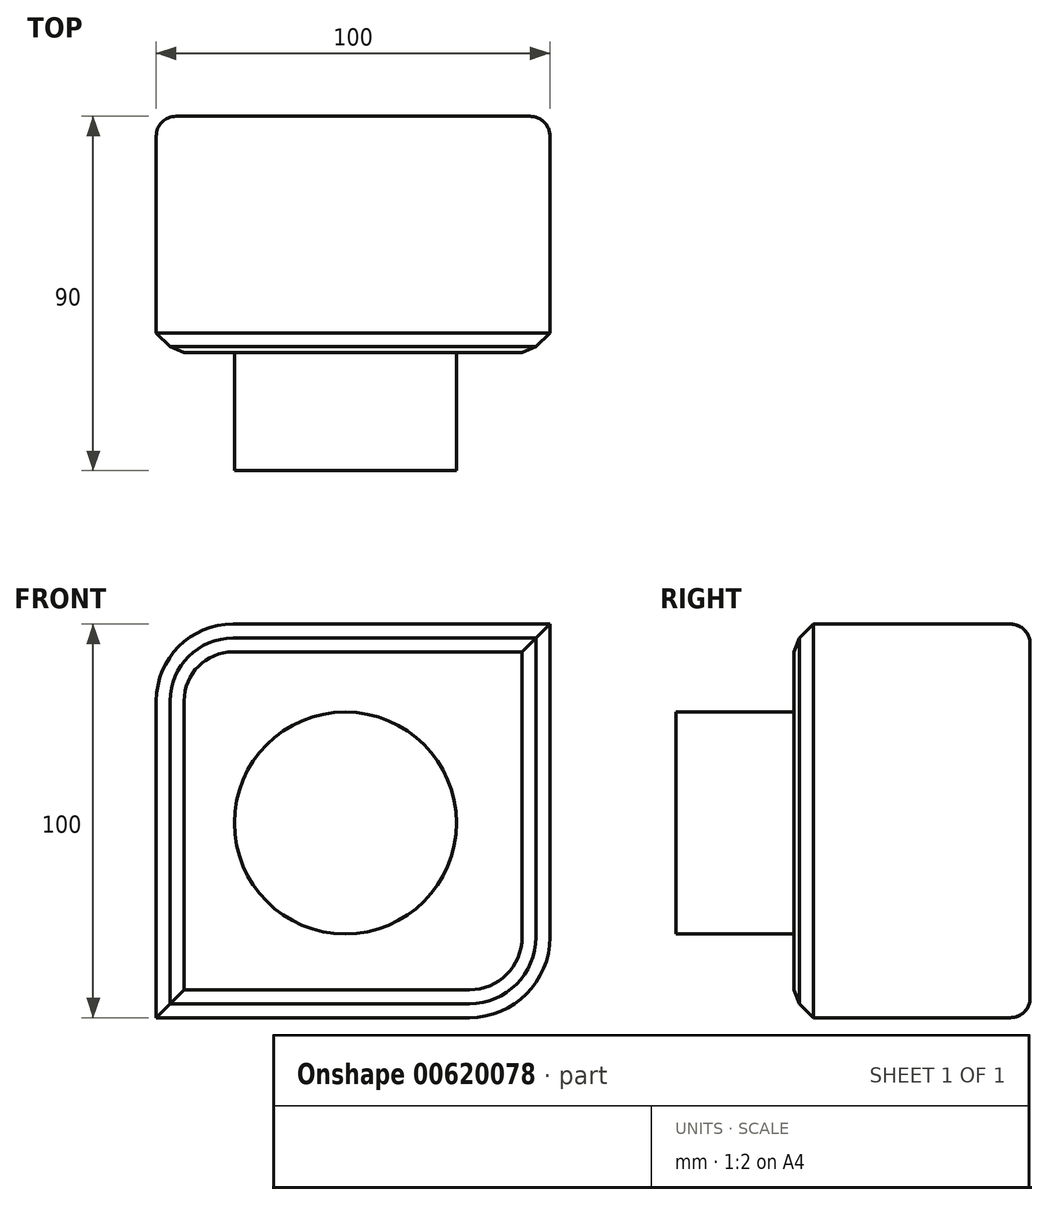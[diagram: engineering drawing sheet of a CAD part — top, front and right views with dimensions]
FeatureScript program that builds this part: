
annotation { "Feature Type Name" : "Feature", "Feature Type Description" : "" }
export const myFeature = defineFeature(function(context is Context, id is Id, definition is map)
    precondition{}
    {
        {
            var Q0;
            Q0=qCreatedBy(makeId("Front.planeOp"),FACE);
            var sketch = newSketch(context, id + "F0", { "sketchPlane" : qUnion([Q0])});
            skLineSegment(sketch, "E0.bottom", {"start": v(-28.55, 50.54) * mm, "end": v(31.41, 50.54) * mm});
            skLineSegment(sketch, "E0.top", {"start": v(-48.04, -49.46) * mm, "end": v(31.52, -49.46) * mm});
            skLineSegment(sketch, "E0.left", {"start": v(-48.04, 31.05) * mm, "end": v(-48.04, -49.46) * mm});
            skLineSegment(sketch, "E0.right", {"start": v(51.96, 29.99) * mm, "end": v(51.96, -29.03) * mm});
            skPoint(sketch, "E1.visualSharp", {"position": v(-48.04, 50.54) * mm});
            skArc(sketch, "E1.filletArc", {"start": v(-28.55, 50.54) * mm, "mid": v(-42.33, 44.83) * mm, "end": v(-48.04, 31.05) * mm});
            skPoint(sketch, "E2.visualSharp", {"position": v(51.96, 50.54) * mm});
            skPoint(sketch, "E3.visualSharp", {"position": v(51.96, -49.46) * mm});
            skArc(sketch, "E3.filletArc", {"start": v(31.52, -49.46) * mm, "mid": v(45.98, -43.48) * mm, "end": v(51.96, -29.03) * mm});
            skLineSegment(sketch, "E4", {"start": v(31.41, 50.54) * mm, "end": v(51.96, 50.54) * mm});
            skLineSegment(sketch, "E5", {"start": v(51.96, 29.99) * mm, "end": v(51.96, 50.54) * mm});
            skSolve(sketch);
        }
        {
            var Q0;
            Q0=makeQuery(id+"F0.imprint","IMPRINT",FACE,{"disambiguationData":[TD([[makeQuery(id+"F0.imprint","IMPRINT",EDGE,{"derivedFrom":sQuery(id+"F0.wireOp",EDGE,"E0.bottom")}),-1.0]])]});
            extrude(context, id + "F1", {"entities" : qUnion([Q0]), "depth" : 60 * mm, "offsetDistance" : 25 * mm});
        }
        {
            var Q0;
            Q0=makeQuery(id+"F1.opExtrude","CAP_FACE",FACE,{"disambiguationData":[OSD([sQuery(id+"F0.wireOp",EDGE,"E0.bottom"),sQuery(id+"F0.wireOp",EDGE,"E0.top"),sQuery(id+"F0.wireOp",EDGE,"E0.left"),sQuery(id+"F0.wireOp",EDGE,"E0.right"),sQuery(id+"F0.wireOp",EDGE,"E1.filletArc"),sQuery(id+"F0.wireOp",EDGE,"E3.filletArc"),sQuery(id+"F0.wireOp",EDGE,"E4"),sQuery(id+"F0.wireOp",EDGE,"E5")])],"isStart":true});
            fillet(context, id + "F2", {"entities" : qUnion([Q0]), "radius" : 5 * mm, "tangentPropagation" : true, "allowEdgeOverflow" : false});
        }
        {
            var Q0;
            Q0=makeQuery(id+"F1.opExtrude","CAP_FACE",FACE,{"disambiguationData":[OSD([sQuery(id+"F0.wireOp",EDGE,"E0.bottom"),sQuery(id+"F0.wireOp",EDGE,"E0.top"),sQuery(id+"F0.wireOp",EDGE,"E0.left"),sQuery(id+"F0.wireOp",EDGE,"E0.right"),sQuery(id+"F0.wireOp",EDGE,"E1.filletArc"),sQuery(id+"F0.wireOp",EDGE,"E3.filletArc"),sQuery(id+"F0.wireOp",EDGE,"E4"),sQuery(id+"F0.wireOp",EDGE,"E5")])],"isStart":false});
            chamfer(context, id + "F3", {"entities" : qUnion([Q0]), "width" : 5 * mm, "tangentPropagation" : true});
        }
        {
            var Q0;
            Q0=makeQuery(id+"F1.opExtrude","CAP_FACE",FACE,{"disambiguationData":[OSD([sQuery(id+"F0.wireOp",EDGE,"E0.bottom"),sQuery(id+"F0.wireOp",EDGE,"E0.top"),sQuery(id+"F0.wireOp",EDGE,"E0.left"),sQuery(id+"F0.wireOp",EDGE,"E0.right"),sQuery(id+"F0.wireOp",EDGE,"E1.filletArc"),sQuery(id+"F0.wireOp",EDGE,"E3.filletArc"),sQuery(id+"F0.wireOp",EDGE,"E4"),sQuery(id+"F0.wireOp",EDGE,"E5")])],"isStart":false});
            chamfer(context, id + "F4", {"entities" : qUnion([Q0]), "width" : 5 * mm, "tangentPropagation" : true});
        }
        {
            var Q0;
            Q0=makeQuery(id+"F1.opExtrude","CAP_FACE",FACE,{"disambiguationData":[OSD([sQuery(id+"F0.wireOp",EDGE,"E0.bottom"),sQuery(id+"F0.wireOp",EDGE,"E0.top"),sQuery(id+"F0.wireOp",EDGE,"E0.left"),sQuery(id+"F0.wireOp",EDGE,"E0.right"),sQuery(id+"F0.wireOp",EDGE,"E1.filletArc"),sQuery(id+"F0.wireOp",EDGE,"E3.filletArc"),sQuery(id+"F0.wireOp",EDGE,"E4"),sQuery(id+"F0.wireOp",EDGE,"E5")])],"isStart":false});
            var sketch = newSketch(context, id + "F5", { "sketchPlane" : qUnion([Q0])});
            skCircle(sketch, "E6", {"center": v(0, 0) * mm, "radius": 28.2 * mm});
            skSolve(sketch);
        }
        {
            var Q0;
            Q0=makeQuery(id+"F5.imprint","IMPRINT",FACE,{"disambiguationData":[TD([[makeQuery(id+"F5.imprint","IMPRINT",EDGE,{"derivedFrom":sQuery(id+"F5.wireOp",EDGE,"E6")}),1.0]])]});
            extrude(context, id + "F6", {"entities" : qUnion([Q0]), "operationType" : NewBodyOperationType.ADD, "depth" : 30 * mm, "offsetDistance" : 25 * mm});
        }
    });
